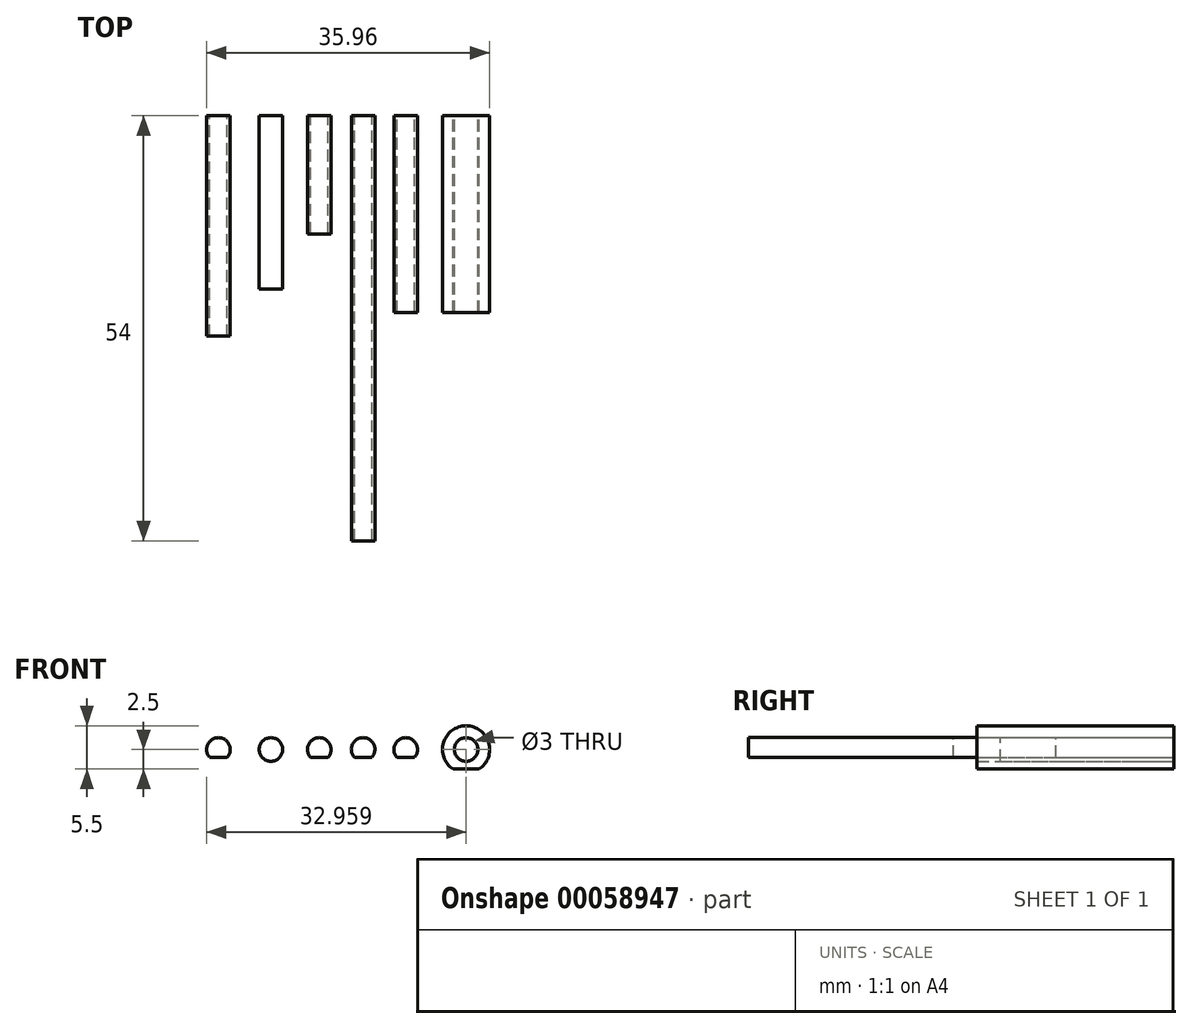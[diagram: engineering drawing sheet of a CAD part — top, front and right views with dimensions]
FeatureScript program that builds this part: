
annotation { "Feature Type Name" : "Feature", "Feature Type Description" : "" }
export const myFeature = defineFeature(function(context is Context, id is Id, definition is map)
    precondition{}
    {
        {
            var Q0;
            Q0=qCreatedBy(makeId("Front.planeOp"),FACE);
            var sketch = newSketch(context, id + "F0", { "sketchPlane" : qUnion([Q0])});
            skLineSegment(sketch, "E0", {"start": v(-14.5, 0) * mm, "end": v(26.86, 0) * mm, "construction": true});
            skLineSegment(sketch, "E1", {"start": v(-9.7, 3.28) * mm, "end": v(-9.7, -4.44) * mm, "construction": true});
            skCircle(sketch, "E2", {"center": v(-9.7, 0) * mm, "radius": 1.5 * mm});
            skPoint(sketch, "E3", {"position": v(-9.7, -1) * mm});
            skLineSegment(sketch, "E4", {"start": v(-10.82, -1) * mm, "end": v(-8.59, -1) * mm});
            skCircle(sketch, "E5", {"center": v(-3.04, 0) * mm, "radius": 1.5 * mm});
            skPoint(sketch, "E6", {"position": v(3.1, -1) * mm});
            skLineSegment(sketch, "E7", {"start": v(1.99, -1) * mm, "end": v(4.22, -1) * mm});
            skCircle(sketch, "E8", {"center": v(3.1, 0) * mm, "radius": 1.5 * mm});
            skLineSegment(sketch, "E9", {"start": v(7.55, -1) * mm, "end": v(9.79, -1) * mm});
            skCircle(sketch, "E10", {"center": v(8.67, 0) * mm, "radius": 1.5 * mm});
            skPoint(sketch, "E11", {"position": v(8.67, -1) * mm});
            skCircle(sketch, "E12", {"center": v(14.08, 0) * mm, "radius": 1.5 * mm});
            skLineSegment(sketch, "E13", {"start": v(12.96, -1) * mm, "end": v(15.2, -1) * mm});
            skPoint(sketch, "E14", {"position": v(14.08, -1) * mm});
            skCircle(sketch, "E15", {"center": v(21.75, 0) * mm, "radius": 1.5 * mm});
            skCircle(sketch, "E16", {"center": v(21.75, 0) * mm, "radius": 3 * mm});
            skLineSegment(sketch, "E17", {"start": v(21.75, 3) * mm, "end": v(21.75, -2.5) * mm, "construction": true});
            skLineSegment(sketch, "E18", {"start": v(20.1, -2.5) * mm, "end": v(23.4, -2.5) * mm});
            skSolve(sketch);
        }
        {
            var Q0;
            {var subQ0=sQuery(id+"F0.wireOp",EDGE,"E4");Q0=makeQuery(id+"F0.imprint","IMPRINT",FACE,{"disambiguationData":[TD([[makeQuery(id+"F0.imprint","IMPRINT",EDGE,{"derivedFrom":subQ0}),1.0]])]});}
            extrude(context, id + "F1", {"entities" : qUnion([Q0]), "depth" : 28 * mm});
        }
        {
            var Q0;
            Q0=makeQuery(id+"F0.imprint","IMPRINT",FACE,{"disambiguationData":[TD([[makeQuery(id+"F0.imprint","IMPRINT",EDGE,{"derivedFrom":sQuery(id+"F0.wireOp",EDGE,"E5")}),1.0]])]});
            extrude(context, id + "F2", {"entities" : qUnion([Q0]), "depth" : 22 * mm});
        }
        {
            var Q0;
            {var subQ0=sQuery(id+"F0.wireOp",EDGE,"E7");Q0=makeQuery(id+"F0.imprint","IMPRINT",FACE,{"disambiguationData":[TD([[makeQuery(id+"F0.imprint","IMPRINT",EDGE,{"derivedFrom":subQ0}),1.0]])]});}
            extrude(context, id + "F3", {"entities" : qUnion([Q0]), "depth" : 15 * mm});
        }
        {
            var Q0;
            {var subQ0=sQuery(id+"F0.wireOp",EDGE,"E9");Q0=makeQuery(id+"F0.imprint","IMPRINT",FACE,{"disambiguationData":[TD([[makeQuery(id+"F0.imprint","IMPRINT",EDGE,{"derivedFrom":subQ0}),1.0]])]});}
            extrude(context, id + "F4", {"entities" : qUnion([Q0]), "depth" : (35 + 19) * mm});
        }
        {
            var Q0;
            {var subQ0=sQuery(id+"F0.wireOp",EDGE,"E13");Q0=makeQuery(id+"F0.imprint","IMPRINT",FACE,{"disambiguationData":[TD([[makeQuery(id+"F0.imprint","IMPRINT",EDGE,{"derivedFrom":subQ0}),1.0]])]});}
            extrude(context, id + "F5", {"entities" : qUnion([Q0]), "depth" : 25 * mm});
        }
        {
            var Q0;
            Q0=makeQuery(id+"F0.imprint","IMPRINT",FACE,{"disambiguationData":[TD([[makeQuery(id+"F0.imprint","IMPRINT",EDGE,{"derivedFrom":sQuery(id+"F0.wireOp",EDGE,"E15")}),-1.0]])]});
            extrude(context, id + "F6", {"entities" : qUnion([Q0]), "depth" : 25 * mm});
        }
    });
